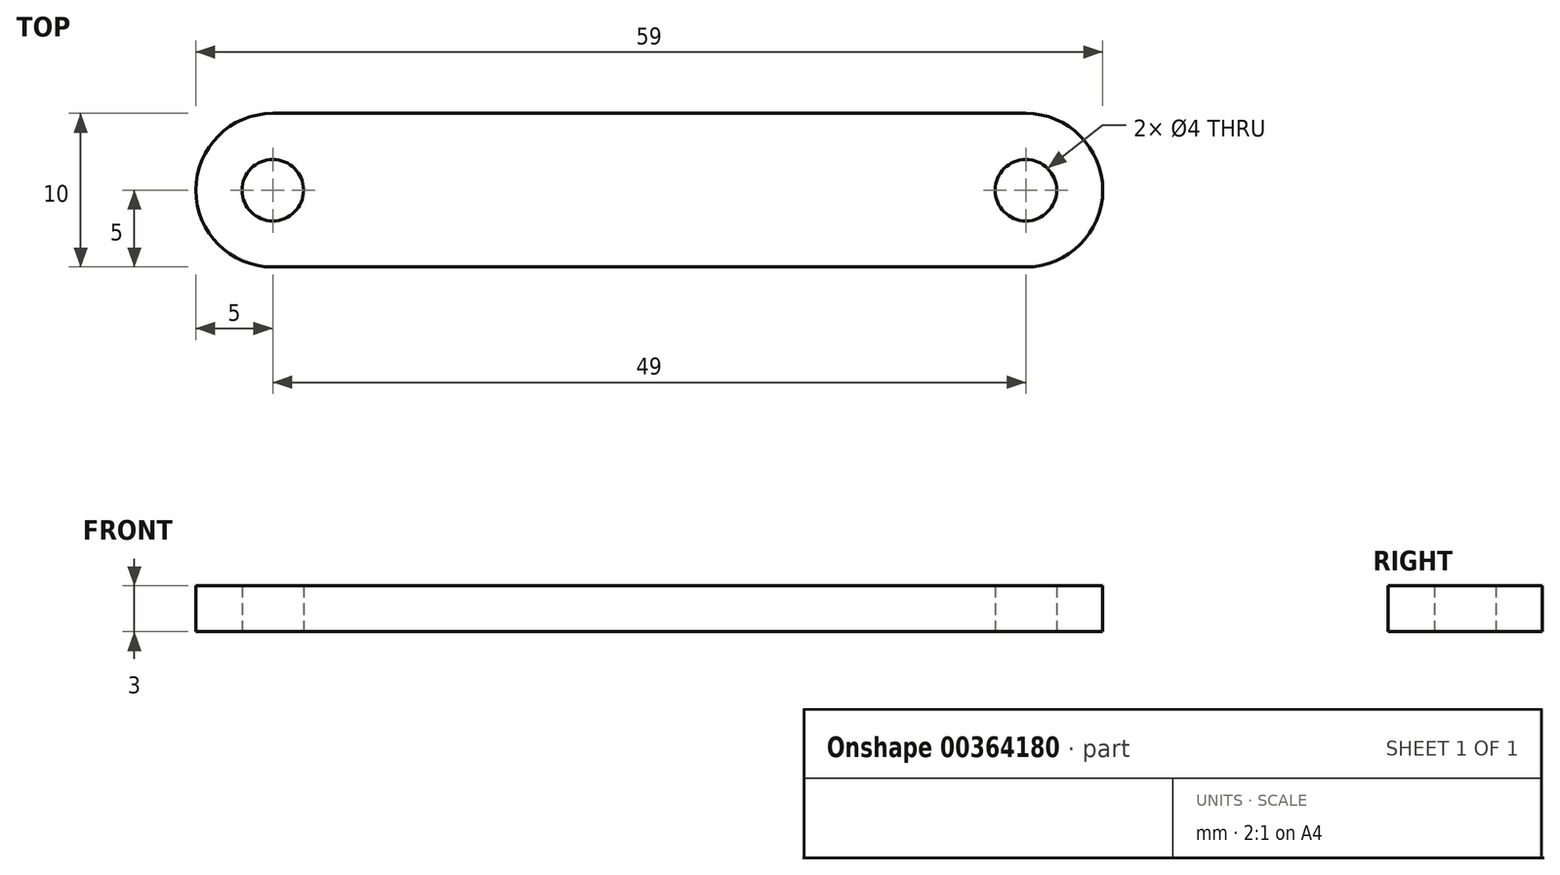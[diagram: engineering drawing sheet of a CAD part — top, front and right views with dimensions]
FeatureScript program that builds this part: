
annotation { "Feature Type Name" : "Feature", "Feature Type Description" : "" }
export const myFeature = defineFeature(function(context is Context, id is Id, definition is map)
    precondition{}
    {
        {
            var Q0;
            Q0=qCreatedBy(makeId("Top.planeOp"),FACE);
            var sketch = newSketch(context, id + "F0", { "sketchPlane" : qUnion([Q0])});
            skLineSegment(sketch, "E0.bottom", {"start": v(24.5, 5) * mm, "end": v(-24.5, 5) * mm});
            skLineSegment(sketch, "E0.top", {"start": v(24.5, -5) * mm, "end": v(-24.5, -5) * mm});
            skPoint(sketch, "E0.middle", {"position": v(0, 0) * mm});
            skCircle(sketch, "E1", {"center": v(-24.5, 0) * mm, "radius": 2 * mm});
            skCircle(sketch, "E2", {"center": v(24.5, 0) * mm, "radius": 2 * mm});
            skArc(sketch, "E3", {"start": v(-24.5, 5) * mm, "mid": v(-29.5, 0) * mm, "end": v(-24.5, -5) * mm});
            skArc(sketch, "E4", {"start": v(24.5, -5) * mm, "mid": v(29.5, 0) * mm, "end": v(24.5, 5) * mm});
            skSolve(sketch);
        }
        {
            var Q0;
            Q0=qSketchRegion(id+"F0",true);
            extrude(context, id + "F1", {"entities" : qUnion([Q0]), "depth" : 3 * mm});
        }
    });
